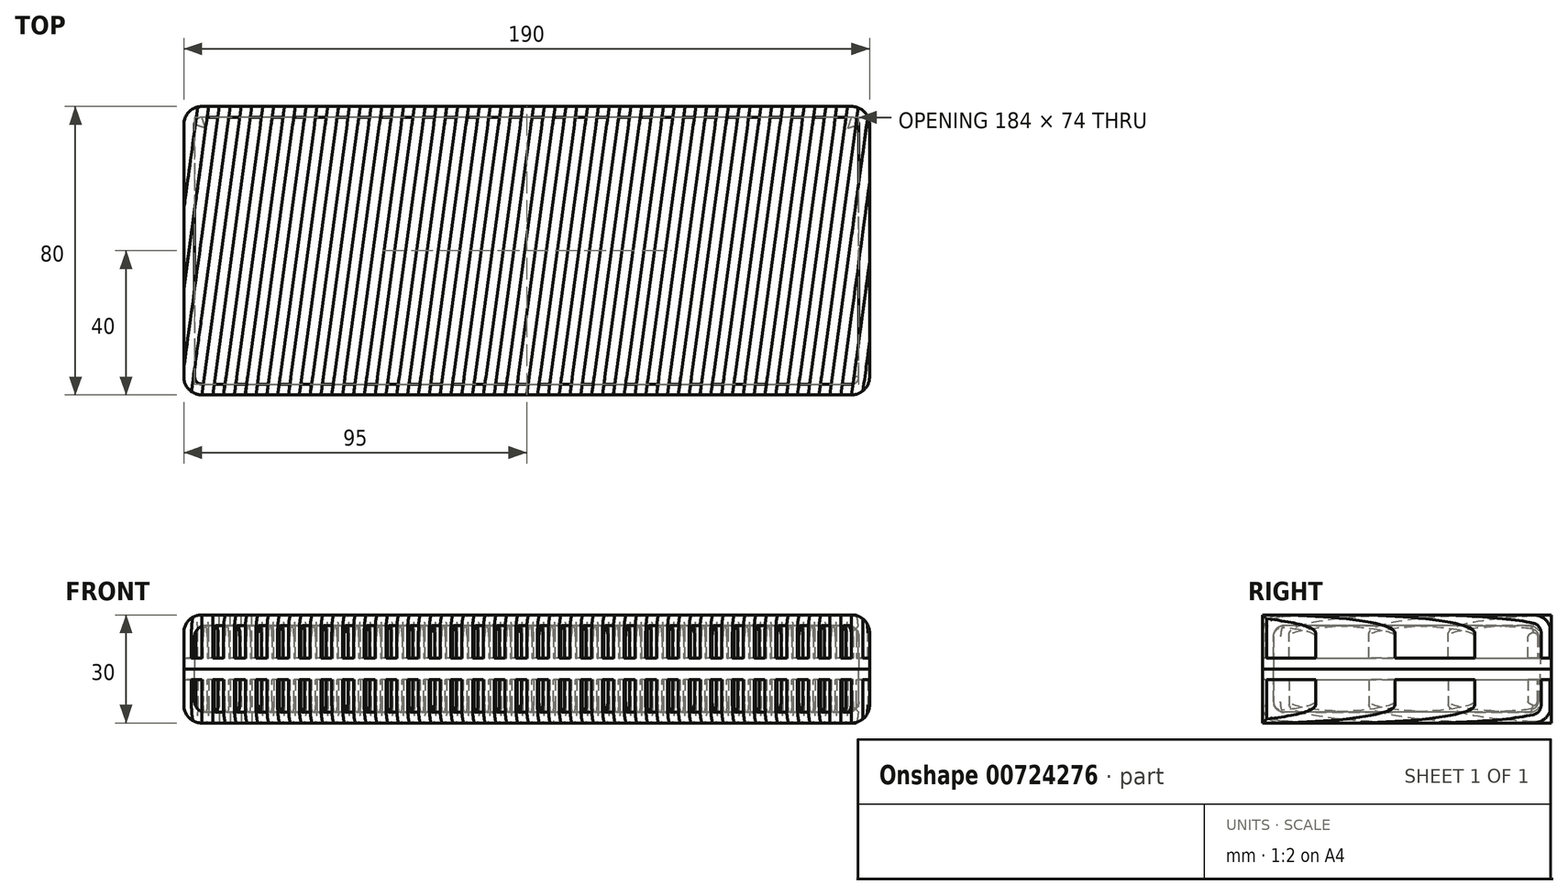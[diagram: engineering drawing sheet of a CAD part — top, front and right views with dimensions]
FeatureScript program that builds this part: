
annotation { "Feature Type Name" : "Feature", "Feature Type Description" : "" }
export const myFeature = defineFeature(function(context is Context, id is Id, definition is map)
    precondition{}
    {
        {
            var Q0;
            Q0=qCreatedBy(makeId("Top.planeOp"),FACE);
            var sketch = newSketch(context, id + "F0", { "sketchPlane" : qUnion([Q0])});
            skLineSegment(sketch, "E0.bottom", {"start": v(90, -40) * mm, "end": v(-90, -40) * mm});
            skLineSegment(sketch, "E0.top", {"start": v(90, 40) * mm, "end": v(-90, 40) * mm});
            skLineSegment(sketch, "E0.left", {"start": v(95, -35) * mm, "end": v(95, 35) * mm});
            skLineSegment(sketch, "E0.right", {"start": v(-95, -35) * mm, "end": v(-95, 35) * mm});
            skPoint(sketch, "E0.middle", {"position": v(0, 0) * mm});
            skPoint(sketch, "E1.visualSharp", {"position": v(-95, 40) * mm});
            skArc(sketch, "E1.filletArc", {"start": v(-90, 40) * mm, "mid": v(-93.54, 38.54) * mm, "end": v(-95, 35) * mm});
            skPoint(sketch, "E2.visualSharp", {"position": v(-95, -40) * mm});
            skArc(sketch, "E2.filletArc", {"start": v(-95, -35) * mm, "mid": v(-93.54, -38.54) * mm, "end": v(-90, -40) * mm});
            skPoint(sketch, "E3.visualSharp", {"position": v(95, -40) * mm});
            skArc(sketch, "E3.filletArc", {"start": v(90, -40) * mm, "mid": v(93.54, -38.54) * mm, "end": v(95, -35) * mm});
            skPoint(sketch, "E4.visualSharp", {"position": v(95, 40) * mm});
            skArc(sketch, "E4.filletArc", {"start": v(95, 35) * mm, "mid": v(93.54, 38.54) * mm, "end": v(90, 40) * mm});
            skSolve(sketch);
        }
        {
            var Q0;
            Q0=makeQuery(id+"F0.imprint","IMPRINT",FACE,{"disambiguationData":[TD([[makeQuery(id+"F0.imprint","IMPRINT",EDGE,{"derivedFrom":sQuery(id+"F0.wireOp",EDGE,"E0.bottom")}),-1.0]])]});
            extrude(context, id + "F1", {"entities" : qUnion([Q0]), "depth" : 15 * mm, "offsetDistance" : 25 * mm});
        }
        {
            var Q0;
            Q0=makeQuery(id+"F1.opExtrude","CAP_FACE",FACE,{"disambiguationData":[OSD([sQuery(id+"F0.wireOp",EDGE,"E0.bottom"),sQuery(id+"F0.wireOp",EDGE,"E0.top"),sQuery(id+"F0.wireOp",EDGE,"E0.left"),sQuery(id+"F0.wireOp",EDGE,"E0.right"),sQuery(id+"F0.wireOp",EDGE,"E1.filletArc"),sQuery(id+"F0.wireOp",EDGE,"E2.filletArc"),sQuery(id+"F0.wireOp",EDGE,"E3.filletArc"),sQuery(id+"F0.wireOp",EDGE,"E4.filletArc")])],"isStart":false});
            var sketch = newSketch(context, id + "F2", { "sketchPlane" : qUnion([Q0])});
            skLineSegment(sketch, "E5.0", {"start": v(92, -35) * mm, "end": v(92, 35) * mm});
            skArc(sketch, "E5.1", {"start": v(90, -37) * mm, "mid": v(91.41, -36.41) * mm, "end": v(92, -35) * mm});
            skArc(sketch, "E5.2", {"start": v(92, 35) * mm, "mid": v(91.41, 36.41) * mm, "end": v(90, 37) * mm});
            skLineSegment(sketch, "E5.3", {"start": v(-90, -37) * mm, "end": v(90, -37) * mm});
            skLineSegment(sketch, "E5.4", {"start": v(90, 37) * mm, "end": v(-90, 37) * mm});
            skArc(sketch, "E5.5", {"start": v(-90, 37) * mm, "mid": v(-91.41, 36.41) * mm, "end": v(-92, 35) * mm});
            skLineSegment(sketch, "E5.6", {"start": v(-92, 35) * mm, "end": v(-92, -35) * mm});
            skArc(sketch, "E5.7", {"start": v(-92, -35) * mm, "mid": v(-91.41, -36.41) * mm, "end": v(-90, -37) * mm});
            skSolve(sketch);
        }
        {
            var Q0;
            Q0=makeQuery(id+"F2.imprint","IMPRINT",FACE,{"disambiguationData":[TD([[makeQuery(id+"F2.imprint","IMPRINT",EDGE,{"derivedFrom":sQuery(id+"F2.wireOp",EDGE,"E5.0")}),1.0]])]});
            extrude(context, id + "F3", {"entities" : qUnion([Q0]), "operationType" : NewBodyOperationType.REMOVE, "oppositeDirection" : true, "depth" : 12 * mm, "offsetDistance" : 25 * mm});
        }
        {
            var Q0;
            Q0=makeQuery(id+"F3.boolean.opBoolean","COPY",EDGE,{"derivedFrom":makeQuery(id+"F3.opExtrude","CAP_EDGE",EDGE,{"disambiguationData":[OSD([sQuery(id+"F2.wireOp",EDGE,"E5.4")])],"isStart":false})});
            var Q1;
            Q1=makeQuery(id+"F3.boolean.opBoolean","COPY",EDGE,{"derivedFrom":makeQuery(id+"F3.opExtrude","CAP_EDGE",EDGE,{"disambiguationData":[OSD([sQuery(id+"F2.wireOp",EDGE,"E5.6")])],"isStart":false})});
            var Q2;
            Q2=makeQuery(id+"F3.boolean.opBoolean","COPY",EDGE,{"derivedFrom":makeQuery(id+"F3.opExtrude","CAP_EDGE",EDGE,{"disambiguationData":[OSD([sQuery(id+"F2.wireOp",EDGE,"E5.3")])],"isStart":false})});
            var Q3;
            Q3=makeQuery(id+"F3.boolean.opBoolean","COPY",EDGE,{"derivedFrom":makeQuery(id+"F3.opExtrude","CAP_EDGE",EDGE,{"disambiguationData":[OSD([sQuery(id+"F2.wireOp",EDGE,"E5.0")])],"isStart":false})});
            fillet(context, id + "F4", {"entities" : qUnion([Q0, Q1, Q2, Q3]), "radius" : 3 * mm, "tangentPropagation" : true, "allowEdgeOverflow" : false});
        }
        {
            var Q0;
            Q0=makeQuery(id+"F3.boolean.opBoolean","COPY",FACE,{"derivedFrom":makeQuery(id+"F3.opExtrude","CAP_FACE",FACE,{"disambiguationData":[OSD([sQuery(id+"F2.wireOp",EDGE,"E5.0"),sQuery(id+"F2.wireOp",EDGE,"E5.1"),sQuery(id+"F2.wireOp",EDGE,"E5.2"),sQuery(id+"F2.wireOp",EDGE,"E5.3"),sQuery(id+"F2.wireOp",EDGE,"E5.4"),sQuery(id+"F2.wireOp",EDGE,"E5.5"),sQuery(id+"F2.wireOp",EDGE,"E5.6"),sQuery(id+"F2.wireOp",EDGE,"E5.7")])],"isStart":false})});
            var sketch = newSketch(context, id + "F5", { "sketchPlane" : qUnion([Q0])});
            skLineSegment(sketch, "E6", {"start": v(89, 0) * mm, "end": v(44.92, 0) * mm, "construction": true});
            skPoint(sketch, "E7", {"position": v(44.92, 0) * mm});
            skCircle(sketch, "E8", {"center": v(44.92, 0) * mm, "radius": 24 * mm, "construction": true});
            skPoint(sketch, "E9", {"position": v(68.93, 0) * mm});
            skLineSegment(sketch, "E10", {"start": v(68.93, 0) * mm, "end": v(65.93, 11.62) * mm, "construction": true});
            skLineSegment(sketch, "E11", {"start": v(65.93, 11.62) * mm, "end": v(57.69, 20.34) * mm, "construction": true});
            skLineSegment(sketch, "E12", {"start": v(57.69, 20.34) * mm, "end": v(46.25, 23.97) * mm, "construction": true});
            skLineSegment(sketch, "E13", {"start": v(46.25, 23.97) * mm, "end": v(34.48, 21.62) * mm, "construction": true});
            skPoint(sketch, "E14", {"position": v(65.93, 11.62) * mm});
            skPoint(sketch, "E15", {"position": v(57.69, 20.34) * mm});
            skPoint(sketch, "E16", {"position": v(46.25, 23.97) * mm});
            skPoint(sketch, "E17", {"position": v(34.48, 21.62) * mm});
            skLineSegment(sketch, "E18.MirrorCS", {"start": v(68.93, 0) * mm, "end": v(65.93, -11.62) * mm, "construction": true});
            skLineSegment(sketch, "E19.MirrorCS", {"start": v(65.93, -11.62) * mm, "end": v(57.69, -20.34) * mm, "construction": true});
            skLineSegment(sketch, "E20.MirrorCS", {"start": v(57.69, -20.34) * mm, "end": v(46.25, -23.97) * mm, "construction": true});
            skLineSegment(sketch, "E21.MirrorCS", {"start": v(46.25, -23.97) * mm, "end": v(34.48, -21.62) * mm, "construction": true});
            skSolve(sketch);
        }
        {
            var Q0;
            {var subQ0=sQuery(id+"F0.wireOp",EDGE,"E1.filletArc");var subQ1=sQuery(id+"F0.wireOp",EDGE,"E0.top");var subQ2=sQuery(id+"F0.wireOp",EDGE,"E0.right");var subQ3=sQuery(id+"F0.wireOp",EDGE,"E0.bottom");var subQ4=sQuery(id+"F0.wireOp",EDGE,"E2.filletArc");Q0=makeQuery(id+"FFGJoZZdiIJdPJ1_1.boolean.opBoolean","SPLIT",FACE,{"disambiguationData":[TD([makeQuery(id+"F1.opExtrude","SWEPT_FACE",FACE,{"disambiguationData":[OSD([subQ2])]})])],"derivedFrom":makeQuery(id+"F1.opExtrude","CAP_FACE",FACE,{"disambiguationData":[OSD([subQ3,subQ1,sQuery(id+"F0.wireOp",EDGE,"E0.left"),subQ2,subQ0,subQ4,sQuery(id+"F0.wireOp",EDGE,"E3.filletArc"),sQuery(id+"F0.wireOp",EDGE,"E4.filletArc")])],"isStart":true})});}
            var sketch = newSketch(context, id + "F6", { "sketchPlane" : qUnion([Q0])});
            skLineSegment(sketch, "E22", {"start": v(-90, 40) * mm, "end": v(-79.12, -40) * mm});
            skLineSegment(sketch, "E23.1.0.0", {"start": v(-87, 40) * mm, "end": v(-76.12, -40) * mm});
            skLineSegment(sketch, "E23.2.0.0", {"start": v(-84, 40) * mm, "end": v(-73.12, -40) * mm});
            skLineSegment(sketch, "E23.3.0.0", {"start": v(-81, 40) * mm, "end": v(-70.12, -40) * mm});
            skLineSegment(sketch, "E23.4.0.0", {"start": v(-78, 40) * mm, "end": v(-67.12, -40) * mm});
            skLineSegment(sketch, "E23.5.0.0", {"start": v(-75, 40) * mm, "end": v(-64.12, -40) * mm});
            skLineSegment(sketch, "E23.6.0.0", {"start": v(-72, 40) * mm, "end": v(-61.12, -40) * mm});
            skLineSegment(sketch, "E23.7.0.0", {"start": v(-69, 40) * mm, "end": v(-58.12, -40) * mm});
            skLineSegment(sketch, "E23.8.0.0", {"start": v(-66, 40) * mm, "end": v(-55.12, -40) * mm});
            skLineSegment(sketch, "E23.9.0.0", {"start": v(-63, 40) * mm, "end": v(-52.12, -40) * mm});
            skLineSegment(sketch, "E23.10.0.0", {"start": v(-60, 40) * mm, "end": v(-49.12, -40) * mm});
            skLineSegment(sketch, "E23.11.0.0", {"start": v(-57, 40) * mm, "end": v(-46.12, -40) * mm});
            skLineSegment(sketch, "E23.12.0.0", {"start": v(-54, 40) * mm, "end": v(-43.12, -40) * mm});
            skLineSegment(sketch, "E23.13.0.0", {"start": v(-51, 40) * mm, "end": v(-40.12, -40) * mm});
            skLineSegment(sketch, "E23.14.0.0", {"start": v(-48, 40) * mm, "end": v(-37.12, -40) * mm});
            skLineSegment(sketch, "E23.15.0.0", {"start": v(-45, 40) * mm, "end": v(-34.12, -40) * mm});
            skLineSegment(sketch, "E23.16.0.0", {"start": v(-42, 40) * mm, "end": v(-31.12, -40) * mm});
            skLineSegment(sketch, "E23.17.0.0", {"start": v(-39, 40) * mm, "end": v(-28.12, -40) * mm});
            skLineSegment(sketch, "E23.18.0.0", {"start": v(-36, 40) * mm, "end": v(-25.12, -40) * mm});
            skLineSegment(sketch, "E23.19.0.0", {"start": v(-33, 40) * mm, "end": v(-22.12, -40) * mm});
            skLineSegment(sketch, "E23.direction1", {"start": v(-79.12, -40) * mm, "end": v(-76.12, -40) * mm, "construction": true});
            skLineSegment(sketch, "E24.0.20.0", {"start": v(-30, 40) * mm, "end": v(-19.12, -40) * mm});
            skLineSegment(sketch, "E24.0.21.0", {"start": v(-27, 40) * mm, "end": v(-16.12, -40) * mm});
            skLineSegment(sketch, "E24.0.22.0", {"start": v(-24, 40) * mm, "end": v(-13.12, -40) * mm});
            skLineSegment(sketch, "E24.0.23.0", {"start": v(-21, 40) * mm, "end": v(-10.12, -40) * mm});
            skLineSegment(sketch, "E24.0.24.0", {"start": v(-18, 40) * mm, "end": v(-7.12, -40) * mm});
            skLineSegment(sketch, "E24.0.25.0", {"start": v(-15, 40) * mm, "end": v(-4.12, -40) * mm});
            skLineSegment(sketch, "E24.0.26.0", {"start": v(-12, 40) * mm, "end": v(-1.12, -40) * mm});
            skLineSegment(sketch, "E24.0.27.0", {"start": v(-9, 40) * mm, "end": v(1.88, -40) * mm});
            skLineSegment(sketch, "E24.0.28.0", {"start": v(-6, 40) * mm, "end": v(4.88, -40) * mm});
            skLineSegment(sketch, "E24.0.29.0", {"start": v(-3, 40) * mm, "end": v(7.88, -40) * mm});
            skLineSegment(sketch, "E24.0.30.0", {"start": v(0, 40) * mm, "end": v(10.88, -40) * mm});
            skLineSegment(sketch, "E24.0.31.0", {"start": v(3, 40) * mm, "end": v(13.88, -40) * mm});
            skLineSegment(sketch, "E24.0.32.0", {"start": v(6, 40) * mm, "end": v(16.88, -40) * mm});
            skLineSegment(sketch, "E24.0.33.0", {"start": v(9, 40) * mm, "end": v(19.88, -40) * mm});
            skLineSegment(sketch, "E24.0.34.0", {"start": v(12, 40) * mm, "end": v(22.88, -40) * mm});
            skLineSegment(sketch, "E24.0.35.0", {"start": v(15, 40) * mm, "end": v(25.88, -40) * mm});
            skLineSegment(sketch, "E24.0.36.0", {"start": v(18, 40) * mm, "end": v(28.88, -40) * mm});
            skLineSegment(sketch, "E24.0.37.0", {"start": v(21, 40) * mm, "end": v(31.88, -40) * mm});
            skLineSegment(sketch, "E24.0.38.0", {"start": v(24, 40) * mm, "end": v(34.88, -40) * mm});
            skLineSegment(sketch, "E24.0.39.0", {"start": v(27, 40) * mm, "end": v(37.88, -40) * mm});
            skLineSegment(sketch, "E24.0.40.0", {"start": v(30, 40) * mm, "end": v(40.88, -40) * mm});
            skLineSegment(sketch, "E24.0.41.0", {"start": v(33, 40) * mm, "end": v(43.88, -40) * mm});
            skLineSegment(sketch, "E24.0.42.0", {"start": v(36, 40) * mm, "end": v(46.88, -40) * mm});
            skLineSegment(sketch, "E24.0.43.0", {"start": v(39, 40) * mm, "end": v(49.88, -40) * mm});
            skLineSegment(sketch, "E24.0.44.0", {"start": v(42, 40) * mm, "end": v(52.88, -40) * mm});
            skLineSegment(sketch, "E24.0.45.0", {"start": v(45, 40) * mm, "end": v(55.88, -40) * mm});
            skLineSegment(sketch, "E24.0.46.0", {"start": v(48, 40) * mm, "end": v(58.88, -40) * mm});
            skLineSegment(sketch, "E24.0.47.0", {"start": v(51, 40) * mm, "end": v(61.88, -40) * mm});
            skLineSegment(sketch, "E24.0.48.0", {"start": v(54, 40) * mm, "end": v(64.88, -40) * mm});
            skLineSegment(sketch, "E24.0.49.0", {"start": v(57, 40) * mm, "end": v(67.88, -40) * mm});
            skLineSegment(sketch, "E24.0.50.0", {"start": v(60, 40) * mm, "end": v(70.88, -40) * mm});
            skLineSegment(sketch, "E24.0.51.0", {"start": v(63, 40) * mm, "end": v(73.88, -40) * mm});
            skLineSegment(sketch, "E24.0.52.0", {"start": v(66, 40) * mm, "end": v(76.88, -40) * mm});
            skLineSegment(sketch, "E24.0.53.0", {"start": v(69, 40) * mm, "end": v(79.88, -40) * mm});
            skLineSegment(sketch, "E24.0.54.0", {"start": v(72, 40) * mm, "end": v(82.88, -40) * mm});
            skLineSegment(sketch, "E24.0.55.0", {"start": v(75, 40) * mm, "end": v(85.88, -40) * mm});
            skLineSegment(sketch, "E24.0.56.0", {"start": v(78, 40) * mm, "end": v(88.88, -40) * mm});
            skLineSegment(sketch, "E24.0.57.0", {"start": v(81, 40) * mm, "end": v(91.88, -40) * mm});
            skLineSegment(sketch, "E24.0.58.0", {"start": v(84, 40) * mm, "end": v(94.88, -40) * mm});
            skLineSegment(sketch, "E24.0.59.0", {"start": v(87, 40) * mm, "end": v(97.88, -40) * mm});
            skLineSegment(sketch, "E25.1.0.0", {"start": v(-93, 40) * mm, "end": v(-82.12, -40) * mm});
            skLineSegment(sketch, "E25.2.0.0", {"start": v(-96, 40) * mm, "end": v(-85.12, -40) * mm});
            skLineSegment(sketch, "E25.direction1", {"start": v(-79.12, -40) * mm, "end": v(-82.12, -40) * mm, "construction": true});
            skLineSegment(sketch, "E26.0.60.0", {"start": v(90, 40) * mm, "end": v(100.88, -40) * mm});
            skLineSegment(sketch, "E26.0.61.0", {"start": v(93, 40) * mm, "end": v(103.88, -40) * mm});
            skLineSegment(sketch, "E27.0.3.0", {"start": v(-99, 40) * mm, "end": v(-88.12, -40) * mm});
            skLineSegment(sketch, "E27.0.4.0", {"start": v(-102, 40) * mm, "end": v(-91.12, -40) * mm});
            skSolve(sketch);
        }
        {
            var Q0;
            {var subQ0=sQuery(id+"F6.wireOp",EDGE,"E23.1.0.0");Q0=makeQuery(id+"F6.imprint","IMPRINT",FACE,{"disambiguationData":[TD([[makeQuery(id+"F6.imprint","IMPRINT",EDGE,{"derivedFrom":subQ0}),1.0]])]});}
            var Q1;
            {var subQ0=sQuery(id+"F6.wireOp",EDGE,"E23.3.0.0");Q1=makeQuery(id+"F6.imprint","IMPRINT",FACE,{"disambiguationData":[TD([[makeQuery(id+"F6.imprint","IMPRINT",EDGE,{"derivedFrom":subQ0}),1.0]])]});}
            var Q2;
            {var subQ0=sQuery(id+"F6.wireOp",EDGE,"E23.5.0.0");Q2=makeQuery(id+"F6.imprint","IMPRINT",FACE,{"disambiguationData":[TD([[makeQuery(id+"F6.imprint","IMPRINT",EDGE,{"derivedFrom":subQ0}),1.0]])]});}
            var Q3;
            {var subQ0=sQuery(id+"F6.wireOp",EDGE,"E23.7.0.0");Q3=makeQuery(id+"F6.imprint","IMPRINT",FACE,{"disambiguationData":[TD([[makeQuery(id+"F6.imprint","IMPRINT",EDGE,{"derivedFrom":subQ0}),1.0]])]});}
            var Q4;
            {var subQ0=sQuery(id+"F6.wireOp",EDGE,"E23.9.0.0");Q4=makeQuery(id+"F6.imprint","IMPRINT",FACE,{"disambiguationData":[TD([[makeQuery(id+"F6.imprint","IMPRINT",EDGE,{"derivedFrom":subQ0}),1.0]])]});}
            var Q5;
            {var subQ0=sQuery(id+"F6.wireOp",EDGE,"E23.11.0.0");Q5=makeQuery(id+"F6.imprint","IMPRINT",FACE,{"disambiguationData":[TD([[makeQuery(id+"F6.imprint","IMPRINT",EDGE,{"derivedFrom":subQ0}),1.0]])]});}
            var Q6;
            {var subQ0=sQuery(id+"F6.wireOp",EDGE,"E23.13.0.0");Q6=makeQuery(id+"F6.imprint","IMPRINT",FACE,{"disambiguationData":[TD([[makeQuery(id+"F6.imprint","IMPRINT",EDGE,{"derivedFrom":subQ0}),1.0]])]});}
            var Q7;
            {var subQ0=sQuery(id+"F6.wireOp",EDGE,"E23.15.0.0");Q7=makeQuery(id+"F6.imprint","IMPRINT",FACE,{"disambiguationData":[TD([[makeQuery(id+"F6.imprint","IMPRINT",EDGE,{"derivedFrom":subQ0}),1.0]])]});}
            var Q8;
            {var subQ0=sQuery(id+"F6.wireOp",EDGE,"E23.17.0.0");Q8=makeQuery(id+"F6.imprint","IMPRINT",FACE,{"disambiguationData":[TD([[makeQuery(id+"F6.imprint","IMPRINT",EDGE,{"derivedFrom":subQ0}),1.0]])]});}
            var Q9;
            {var subQ0=sQuery(id+"F6.wireOp",EDGE,"E23.19.0.0");Q9=makeQuery(id+"F6.imprint","IMPRINT",FACE,{"disambiguationData":[TD([[makeQuery(id+"F6.imprint","IMPRINT",EDGE,{"derivedFrom":subQ0}),1.0]])]});}
            var Q10;
            {var subQ0=sQuery(id+"F6.wireOp",EDGE,"E24.0.21.0");Q10=makeQuery(id+"F6.imprint","IMPRINT",FACE,{"disambiguationData":[TD([[makeQuery(id+"F6.imprint","IMPRINT",EDGE,{"derivedFrom":subQ0}),1.0]])]});}
            var Q11;
            {var subQ0=sQuery(id+"F6.wireOp",EDGE,"E24.0.23.0");Q11=makeQuery(id+"F6.imprint","IMPRINT",FACE,{"disambiguationData":[TD([[makeQuery(id+"F6.imprint","IMPRINT",EDGE,{"derivedFrom":subQ0}),1.0]])]});}
            var Q12;
            {var subQ0=sQuery(id+"F6.wireOp",EDGE,"E24.0.25.0");Q12=makeQuery(id+"F6.imprint","IMPRINT",FACE,{"disambiguationData":[TD([[makeQuery(id+"F6.imprint","IMPRINT",EDGE,{"derivedFrom":subQ0}),1.0]])]});}
            var Q13;
            {var subQ0=sQuery(id+"F6.wireOp",EDGE,"E24.0.27.0");Q13=makeQuery(id+"F6.imprint","IMPRINT",FACE,{"disambiguationData":[TD([[makeQuery(id+"F6.imprint","IMPRINT",EDGE,{"derivedFrom":subQ0}),1.0]])]});}
            var Q14;
            {var subQ0=sQuery(id+"F6.wireOp",EDGE,"E24.0.29.0");Q14=makeQuery(id+"F6.imprint","IMPRINT",FACE,{"disambiguationData":[TD([[makeQuery(id+"F6.imprint","IMPRINT",EDGE,{"derivedFrom":subQ0}),1.0]])]});}
            var Q15;
            {var subQ0=sQuery(id+"F6.wireOp",EDGE,"E24.0.31.0");Q15=makeQuery(id+"F6.imprint","IMPRINT",FACE,{"disambiguationData":[TD([[makeQuery(id+"F6.imprint","IMPRINT",EDGE,{"derivedFrom":subQ0}),1.0]])]});}
            var Q16;
            {var subQ0=sQuery(id+"F6.wireOp",EDGE,"E24.0.33.0");Q16=makeQuery(id+"F6.imprint","IMPRINT",FACE,{"disambiguationData":[TD([[makeQuery(id+"F6.imprint","IMPRINT",EDGE,{"derivedFrom":subQ0}),1.0]])]});}
            var Q17;
            {var subQ0=sQuery(id+"F6.wireOp",EDGE,"E24.0.35.0");Q17=makeQuery(id+"F6.imprint","IMPRINT",FACE,{"disambiguationData":[TD([[makeQuery(id+"F6.imprint","IMPRINT",EDGE,{"derivedFrom":subQ0}),1.0]])]});}
            var Q18;
            {var subQ0=sQuery(id+"F6.wireOp",EDGE,"E24.0.37.0");Q18=makeQuery(id+"F6.imprint","IMPRINT",FACE,{"disambiguationData":[TD([[makeQuery(id+"F6.imprint","IMPRINT",EDGE,{"derivedFrom":subQ0}),1.0]])]});}
            var Q19;
            {var subQ0=sQuery(id+"F6.wireOp",EDGE,"E24.0.39.0");Q19=makeQuery(id+"F6.imprint","IMPRINT",FACE,{"disambiguationData":[TD([[makeQuery(id+"F6.imprint","IMPRINT",EDGE,{"derivedFrom":subQ0}),1.0]])]});}
            var Q20;
            {var subQ0=sQuery(id+"F6.wireOp",EDGE,"E24.0.41.0");Q20=makeQuery(id+"F6.imprint","IMPRINT",FACE,{"disambiguationData":[TD([[makeQuery(id+"F6.imprint","IMPRINT",EDGE,{"derivedFrom":subQ0}),1.0]])]});}
            var Q21;
            {var subQ0=sQuery(id+"F6.wireOp",EDGE,"E24.0.43.0");Q21=makeQuery(id+"F6.imprint","IMPRINT",FACE,{"disambiguationData":[TD([[makeQuery(id+"F6.imprint","IMPRINT",EDGE,{"derivedFrom":subQ0}),1.0]])]});}
            var Q22;
            {var subQ0=sQuery(id+"F6.wireOp",EDGE,"E24.0.45.0");Q22=makeQuery(id+"F6.imprint","IMPRINT",FACE,{"disambiguationData":[TD([[makeQuery(id+"F6.imprint","IMPRINT",EDGE,{"derivedFrom":subQ0}),1.0]])]});}
            var Q23;
            {var subQ0=sQuery(id+"F6.wireOp",EDGE,"E24.0.47.0");Q23=makeQuery(id+"F6.imprint","IMPRINT",FACE,{"disambiguationData":[TD([[makeQuery(id+"F6.imprint","IMPRINT",EDGE,{"derivedFrom":subQ0}),1.0]])]});}
            var Q24;
            {var subQ0=sQuery(id+"F6.wireOp",EDGE,"E24.0.49.0");Q24=makeQuery(id+"F6.imprint","IMPRINT",FACE,{"disambiguationData":[TD([[makeQuery(id+"F6.imprint","IMPRINT",EDGE,{"derivedFrom":subQ0}),1.0]])]});}
            var Q25;
            {var subQ0=sQuery(id+"F6.wireOp",EDGE,"E24.0.51.0");Q25=makeQuery(id+"F6.imprint","IMPRINT",FACE,{"disambiguationData":[TD([[makeQuery(id+"F6.imprint","IMPRINT",EDGE,{"derivedFrom":subQ0}),1.0]])]});}
            var Q26;
            {var subQ0=sQuery(id+"F6.wireOp",EDGE,"E24.0.53.0");Q26=makeQuery(id+"F6.imprint","IMPRINT",FACE,{"disambiguationData":[TD([[makeQuery(id+"F6.imprint","IMPRINT",EDGE,{"derivedFrom":subQ0}),1.0]])]});}
            var Q27;
            {var subQ0=sQuery(id+"F6.wireOp",EDGE,"E24.0.55.0");Q27=makeQuery(id+"F6.imprint","IMPRINT",FACE,{"disambiguationData":[TD([[makeQuery(id+"F6.imprint","IMPRINT",EDGE,{"derivedFrom":subQ0}),1.0]])]});}
            var Q28;
            {var subQ0=sQuery(id+"F6.wireOp",EDGE,"E24.0.57.0");var subQ1=makeQuery(id+"F1.opExtrude","CAP_EDGE",EDGE,{"disambiguationData":[OSD([sQuery(id+"F0.wireOp",EDGE,"E0.bottom")])],"isStart":true});var subQ2=makeQuery(id+"F6.imprint","INTERSECT",VERTEX,{"derivedFrom":[subQ1,subQ0]});Q28=makeQuery(id+"F6.imprint","IMPRINT",FACE,{"disambiguationData":[TD([[makeQuery(id+"F6.imprint","IMPRINT",EDGE,{"disambiguationData":[TD([[subQ2,-1.0]])],"derivedFrom":subQ0}),1.0]])]});}
            var Q29;
            {var subQ0=sQuery(id+"F6.wireOp",EDGE,"E22");Q29=makeQuery(id+"F6.imprint","IMPRINT",FACE,{"disambiguationData":[TD([[makeQuery(id+"F6.imprint","IMPRINT",EDGE,{"derivedFrom":subQ0}),-1.0]])]});}
            var Q30;
            {var subQ0=sQuery(id+"F6.wireOp",EDGE,"E25.2.0.0");var subQ1=makeQuery(id+"F1.opExtrude","CAP_EDGE",EDGE,{"disambiguationData":[OSD([sQuery(id+"F0.wireOp",EDGE,"E0.top")])],"isStart":true});var subQ2=makeQuery(id+"F6.imprint","INTERSECT",VERTEX,{"derivedFrom":[subQ1,subQ0]});Q30=makeQuery(id+"F6.imprint","IMPRINT",FACE,{"disambiguationData":[TD([[makeQuery(id+"F6.imprint","IMPRINT",EDGE,{"disambiguationData":[TD([[subQ2,1.0]])],"derivedFrom":subQ0}),-1.0]])]});}
            var Q31;
            {var subQ0=sQuery(id+"F6.wireOp",EDGE,"E27.0.4.0");var subQ1=makeQuery(id+"F1.opExtrude","CAP_EDGE",EDGE,{"disambiguationData":[OSD([sQuery(id+"F0.wireOp",EDGE,"E1.filletArc")])],"isStart":true});var subQ2=makeQuery(id+"F6.imprint","INTERSECT",VERTEX,{"derivedFrom":[subQ1,subQ0]});Q31=makeQuery(id+"F6.imprint","IMPRINT",FACE,{"disambiguationData":[TD([[makeQuery(id+"F6.imprint","IMPRINT",EDGE,{"disambiguationData":[TD([[subQ2,1.0]])],"derivedFrom":subQ0}),-1.0]])]});}
            var Q32;
            {var subQ0=sQuery(id+"F6.wireOp",EDGE,"E24.0.59.0");var subQ1=makeQuery(id+"F1.opExtrude","CAP_EDGE",EDGE,{"disambiguationData":[OSD([sQuery(id+"F0.wireOp",EDGE,"E0.bottom")])],"isStart":true});var subQ2=makeQuery(id+"F6.imprint","INTERSECT",VERTEX,{"derivedFrom":[subQ1,subQ0]});Q32=makeQuery(id+"F6.imprint","IMPRINT",FACE,{"disambiguationData":[TD([[makeQuery(id+"F6.imprint","IMPRINT",EDGE,{"disambiguationData":[TD([[subQ2,-1.0]])],"derivedFrom":subQ0}),1.0]])]});}
            var Q33;
            {var subQ0=sQuery(id+"F6.wireOp",EDGE,"E26.0.61.0");var subQ1=makeQuery(id+"F1.opExtrude","CAP_EDGE",EDGE,{"disambiguationData":[OSD([sQuery(id+"F0.wireOp",EDGE,"E3.filletArc")])],"isStart":true});var subQ2=makeQuery(id+"F6.imprint","INTERSECT",VERTEX,{"derivedFrom":[subQ1,subQ0]});Q33=makeQuery(id+"F6.imprint","IMPRINT",FACE,{"disambiguationData":[TD([[makeQuery(id+"F6.imprint","IMPRINT",EDGE,{"disambiguationData":[TD([[subQ2,-1.0]])],"derivedFrom":subQ0}),1.0]])]});}
            extrude(context, id + "F7", {"entities" : qUnion([Q0, Q1, Q2, Q3, Q4, Q5, Q6, Q7, Q8, Q9, Q10, Q11, Q12, Q13, Q14, Q15, Q16, Q17, Q18, Q19, Q20, Q21, Q22, Q23, Q24, Q25, Q26, Q27, Q28, Q29, Q30, Q31, Q32, Q33]), "operationType" : NewBodyOperationType.REMOVE, "oppositeDirection" : true, "depth" : 12 * mm, "offsetDistance" : 25 * mm});
        }
        {
            var Q0;
            {var subQ0=sQuery(id+"F0.wireOp",EDGE,"E0.bottom");Q0=makeQuery(id+"F7.boolean.opBoolean","SPLIT",EDGE,{"disambiguationData":[TD([makeQuery(id+"F7.opExtrude","SWEPT_FACE",FACE,{"disambiguationData":[OSD([sQuery(id+"F6.wireOp",EDGE,"E23.2.0.0")])]})])],"derivedFrom":makeQuery(id+"F1.opExtrude","CAP_EDGE",EDGE,{"disambiguationData":[OSD([subQ0])],"isStart":true})});}
            var Q1;
            {var subQ0=sQuery(id+"F0.wireOp",EDGE,"E0.bottom");Q1=makeQuery(id+"F7.boolean.opBoolean","SPLIT",EDGE,{"disambiguationData":[TD([makeQuery(id+"F7.opExtrude","SWEPT_FACE",FACE,{"disambiguationData":[OSD([sQuery(id+"F6.wireOp",EDGE,"E23.4.0.0")])]})])],"derivedFrom":makeQuery(id+"F1.opExtrude","CAP_EDGE",EDGE,{"disambiguationData":[OSD([subQ0])],"isStart":true})});}
            var Q2;
            {var subQ0=sQuery(id+"F0.wireOp",EDGE,"E0.bottom");Q2=makeQuery(id+"F7.boolean.opBoolean","SPLIT",EDGE,{"disambiguationData":[TD([makeQuery(id+"F7.opExtrude","SWEPT_FACE",FACE,{"disambiguationData":[OSD([sQuery(id+"F6.wireOp",EDGE,"E23.6.0.0")])]})])],"derivedFrom":makeQuery(id+"F1.opExtrude","CAP_EDGE",EDGE,{"disambiguationData":[OSD([subQ0])],"isStart":true})});}
            var Q3;
            {var subQ0=sQuery(id+"F0.wireOp",EDGE,"E0.bottom");Q3=makeQuery(id+"F7.boolean.opBoolean","SPLIT",EDGE,{"disambiguationData":[TD([makeQuery(id+"F7.opExtrude","SWEPT_FACE",FACE,{"disambiguationData":[OSD([sQuery(id+"F6.wireOp",EDGE,"E23.8.0.0")])]})])],"derivedFrom":makeQuery(id+"F1.opExtrude","CAP_EDGE",EDGE,{"disambiguationData":[OSD([subQ0])],"isStart":true})});}
            var Q4;
            {var subQ0=sQuery(id+"F0.wireOp",EDGE,"E0.bottom");Q4=makeQuery(id+"F7.boolean.opBoolean","SPLIT",EDGE,{"disambiguationData":[TD([makeQuery(id+"F7.opExtrude","SWEPT_FACE",FACE,{"disambiguationData":[OSD([sQuery(id+"F6.wireOp",EDGE,"E23.10.0.0")])]})])],"derivedFrom":makeQuery(id+"F1.opExtrude","CAP_EDGE",EDGE,{"disambiguationData":[OSD([subQ0])],"isStart":true})});}
            var Q5;
            {var subQ0=sQuery(id+"F0.wireOp",EDGE,"E0.bottom");var subQ1=sQuery(id+"F0.wireOp",EDGE,"E2.filletArc");Q5=makeQuery(id+"F7.boolean.opBoolean","SPLIT",EDGE,{"disambiguationData":[TD([makeQuery(id+"F1.opExtrude","SWEPT_FACE",FACE,{"disambiguationData":[OSD([subQ1])]})])],"derivedFrom":makeQuery(id+"F1.opExtrude","CAP_EDGE",EDGE,{"disambiguationData":[OSD([subQ0])],"isStart":true})});}
            var Q6;
            Q6=makeQuery(id+"F1.opExtrude","CAP_EDGE",EDGE,{"disambiguationData":[OSD([sQuery(id+"F0.wireOp",EDGE,"E0.right")])],"isStart":true});
            var Q7;
            {var subQ0=sQuery(id+"F0.wireOp",EDGE,"E1.filletArc");var subQ1=sQuery(id+"F0.wireOp",EDGE,"E0.top");Q7=makeQuery(id+"F7.boolean.opBoolean","SPLIT",EDGE,{"disambiguationData":[TD([makeQuery(id+"F1.opExtrude","SWEPT_FACE",FACE,{"disambiguationData":[OSD([subQ0])]})])],"derivedFrom":makeQuery(id+"F1.opExtrude","CAP_EDGE",EDGE,{"disambiguationData":[OSD([subQ1])],"isStart":true})});}
            var Q8;
            {var subQ0=sQuery(id+"F0.wireOp",EDGE,"E0.bottom");Q8=makeQuery(id+"F7.boolean.opBoolean","SPLIT",EDGE,{"disambiguationData":[TD([makeQuery(id+"F7.opExtrude","SWEPT_FACE",FACE,{"disambiguationData":[OSD([sQuery(id+"F6.wireOp",EDGE,"E23.12.0.0")])]})])],"derivedFrom":makeQuery(id+"F1.opExtrude","CAP_EDGE",EDGE,{"disambiguationData":[OSD([subQ0])],"isStart":true})});}
            var Q9;
            {var subQ0=sQuery(id+"F0.wireOp",EDGE,"E0.bottom");Q9=makeQuery(id+"F7.boolean.opBoolean","SPLIT",EDGE,{"disambiguationData":[TD([makeQuery(id+"F7.opExtrude","SWEPT_FACE",FACE,{"disambiguationData":[OSD([sQuery(id+"F6.wireOp",EDGE,"E23.14.0.0")])]})])],"derivedFrom":makeQuery(id+"F1.opExtrude","CAP_EDGE",EDGE,{"disambiguationData":[OSD([subQ0])],"isStart":true})});}
            var Q10;
            {var subQ0=sQuery(id+"F0.wireOp",EDGE,"E0.bottom");Q10=makeQuery(id+"F7.boolean.opBoolean","SPLIT",EDGE,{"disambiguationData":[TD([makeQuery(id+"F7.opExtrude","SWEPT_FACE",FACE,{"disambiguationData":[OSD([sQuery(id+"F6.wireOp",EDGE,"E23.16.0.0")])]})])],"derivedFrom":makeQuery(id+"F1.opExtrude","CAP_EDGE",EDGE,{"disambiguationData":[OSD([subQ0])],"isStart":true})});}
            var Q11;
            {var subQ0=sQuery(id+"F0.wireOp",EDGE,"E0.bottom");Q11=makeQuery(id+"F7.boolean.opBoolean","SPLIT",EDGE,{"disambiguationData":[TD([makeQuery(id+"F7.opExtrude","SWEPT_FACE",FACE,{"disambiguationData":[OSD([sQuery(id+"F6.wireOp",EDGE,"E23.18.0.0")])]})])],"derivedFrom":makeQuery(id+"F1.opExtrude","CAP_EDGE",EDGE,{"disambiguationData":[OSD([subQ0])],"isStart":true})});}
            var Q12;
            {var subQ0=sQuery(id+"F0.wireOp",EDGE,"E0.bottom");Q12=makeQuery(id+"F7.boolean.opBoolean","SPLIT",EDGE,{"disambiguationData":[TD([makeQuery(id+"F7.opExtrude","SWEPT_FACE",FACE,{"disambiguationData":[OSD([sQuery(id+"F6.wireOp",EDGE,"E24.0.20.0")])]})])],"derivedFrom":makeQuery(id+"F1.opExtrude","CAP_EDGE",EDGE,{"disambiguationData":[OSD([subQ0])],"isStart":true})});}
            var Q13;
            {var subQ0=sQuery(id+"F0.wireOp",EDGE,"E0.bottom");Q13=makeQuery(id+"F7.boolean.opBoolean","SPLIT",EDGE,{"disambiguationData":[TD([makeQuery(id+"F7.opExtrude","SWEPT_FACE",FACE,{"disambiguationData":[OSD([sQuery(id+"F6.wireOp",EDGE,"E24.0.22.0")])]})])],"derivedFrom":makeQuery(id+"F1.opExtrude","CAP_EDGE",EDGE,{"disambiguationData":[OSD([subQ0])],"isStart":true})});}
            var Q14;
            {var subQ0=sQuery(id+"F0.wireOp",EDGE,"E0.bottom");Q14=makeQuery(id+"F7.boolean.opBoolean","SPLIT",EDGE,{"disambiguationData":[TD([makeQuery(id+"F7.opExtrude","SWEPT_FACE",FACE,{"disambiguationData":[OSD([sQuery(id+"F6.wireOp",EDGE,"E24.0.24.0")])]})])],"derivedFrom":makeQuery(id+"F1.opExtrude","CAP_EDGE",EDGE,{"disambiguationData":[OSD([subQ0])],"isStart":true})});}
            var Q15;
            {var subQ0=sQuery(id+"F0.wireOp",EDGE,"E0.bottom");Q15=makeQuery(id+"F7.boolean.opBoolean","SPLIT",EDGE,{"disambiguationData":[TD([makeQuery(id+"F7.opExtrude","SWEPT_FACE",FACE,{"disambiguationData":[OSD([sQuery(id+"F6.wireOp",EDGE,"E24.0.26.0")])]})])],"derivedFrom":makeQuery(id+"F1.opExtrude","CAP_EDGE",EDGE,{"disambiguationData":[OSD([subQ0])],"isStart":true})});}
            var Q16;
            {var subQ0=sQuery(id+"F0.wireOp",EDGE,"E0.bottom");Q16=makeQuery(id+"F7.boolean.opBoolean","SPLIT",EDGE,{"disambiguationData":[TD([makeQuery(id+"F7.opExtrude","SWEPT_FACE",FACE,{"disambiguationData":[OSD([sQuery(id+"F6.wireOp",EDGE,"E24.0.28.0")])]})])],"derivedFrom":makeQuery(id+"F1.opExtrude","CAP_EDGE",EDGE,{"disambiguationData":[OSD([subQ0])],"isStart":true})});}
            var Q17;
            {var subQ0=sQuery(id+"F0.wireOp",EDGE,"E0.bottom");Q17=makeQuery(id+"F7.boolean.opBoolean","SPLIT",EDGE,{"disambiguationData":[TD([makeQuery(id+"F7.opExtrude","SWEPT_FACE",FACE,{"disambiguationData":[OSD([sQuery(id+"F6.wireOp",EDGE,"E24.0.30.0")])]})])],"derivedFrom":makeQuery(id+"F1.opExtrude","CAP_EDGE",EDGE,{"disambiguationData":[OSD([subQ0])],"isStart":true})});}
            var Q18;
            {var subQ0=sQuery(id+"F0.wireOp",EDGE,"E0.bottom");Q18=makeQuery(id+"F7.boolean.opBoolean","SPLIT",EDGE,{"disambiguationData":[TD([makeQuery(id+"F7.opExtrude","SWEPT_FACE",FACE,{"disambiguationData":[OSD([sQuery(id+"F6.wireOp",EDGE,"E24.0.32.0")])]})])],"derivedFrom":makeQuery(id+"F1.opExtrude","CAP_EDGE",EDGE,{"disambiguationData":[OSD([subQ0])],"isStart":true})});}
            var Q19;
            {var subQ0=sQuery(id+"F0.wireOp",EDGE,"E0.bottom");Q19=makeQuery(id+"F7.boolean.opBoolean","SPLIT",EDGE,{"disambiguationData":[TD([makeQuery(id+"F7.opExtrude","SWEPT_FACE",FACE,{"disambiguationData":[OSD([sQuery(id+"F6.wireOp",EDGE,"E24.0.34.0")])]})])],"derivedFrom":makeQuery(id+"F1.opExtrude","CAP_EDGE",EDGE,{"disambiguationData":[OSD([subQ0])],"isStart":true})});}
            var Q20;
            {var subQ0=sQuery(id+"F0.wireOp",EDGE,"E0.bottom");Q20=makeQuery(id+"F7.boolean.opBoolean","SPLIT",EDGE,{"disambiguationData":[TD([makeQuery(id+"F7.opExtrude","SWEPT_FACE",FACE,{"disambiguationData":[OSD([sQuery(id+"F6.wireOp",EDGE,"E24.0.36.0")])]})])],"derivedFrom":makeQuery(id+"F1.opExtrude","CAP_EDGE",EDGE,{"disambiguationData":[OSD([subQ0])],"isStart":true})});}
            var Q21;
            {var subQ0=sQuery(id+"F0.wireOp",EDGE,"E0.bottom");Q21=makeQuery(id+"F7.boolean.opBoolean","SPLIT",EDGE,{"disambiguationData":[TD([makeQuery(id+"F7.opExtrude","SWEPT_FACE",FACE,{"disambiguationData":[OSD([sQuery(id+"F6.wireOp",EDGE,"E24.0.38.0")])]})])],"derivedFrom":makeQuery(id+"F1.opExtrude","CAP_EDGE",EDGE,{"disambiguationData":[OSD([subQ0])],"isStart":true})});}
            var Q22;
            {var subQ0=sQuery(id+"F0.wireOp",EDGE,"E0.bottom");Q22=makeQuery(id+"F7.boolean.opBoolean","SPLIT",EDGE,{"disambiguationData":[TD([makeQuery(id+"F7.opExtrude","SWEPT_FACE",FACE,{"disambiguationData":[OSD([sQuery(id+"F6.wireOp",EDGE,"E24.0.40.0")])]})])],"derivedFrom":makeQuery(id+"F1.opExtrude","CAP_EDGE",EDGE,{"disambiguationData":[OSD([subQ0])],"isStart":true})});}
            var Q23;
            {var subQ0=sQuery(id+"F0.wireOp",EDGE,"E0.bottom");Q23=makeQuery(id+"F7.boolean.opBoolean","SPLIT",EDGE,{"disambiguationData":[TD([makeQuery(id+"F7.opExtrude","SWEPT_FACE",FACE,{"disambiguationData":[OSD([sQuery(id+"F6.wireOp",EDGE,"E24.0.42.0")])]})])],"derivedFrom":makeQuery(id+"F1.opExtrude","CAP_EDGE",EDGE,{"disambiguationData":[OSD([subQ0])],"isStart":true})});}
            var Q24;
            {var subQ0=sQuery(id+"F0.wireOp",EDGE,"E0.bottom");Q24=makeQuery(id+"F7.boolean.opBoolean","SPLIT",EDGE,{"disambiguationData":[TD([makeQuery(id+"F7.opExtrude","SWEPT_FACE",FACE,{"disambiguationData":[OSD([sQuery(id+"F6.wireOp",EDGE,"E24.0.44.0")])]})])],"derivedFrom":makeQuery(id+"F1.opExtrude","CAP_EDGE",EDGE,{"disambiguationData":[OSD([subQ0])],"isStart":true})});}
            var Q25;
            {var subQ0=sQuery(id+"F0.wireOp",EDGE,"E0.bottom");Q25=makeQuery(id+"F7.boolean.opBoolean","SPLIT",EDGE,{"disambiguationData":[TD([makeQuery(id+"F7.opExtrude","SWEPT_FACE",FACE,{"disambiguationData":[OSD([sQuery(id+"F6.wireOp",EDGE,"E24.0.46.0")])]})])],"derivedFrom":makeQuery(id+"F1.opExtrude","CAP_EDGE",EDGE,{"disambiguationData":[OSD([subQ0])],"isStart":true})});}
            var Q26;
            {var subQ0=sQuery(id+"F0.wireOp",EDGE,"E0.bottom");Q26=makeQuery(id+"F7.boolean.opBoolean","SPLIT",EDGE,{"disambiguationData":[TD([makeQuery(id+"F7.opExtrude","SWEPT_FACE",FACE,{"disambiguationData":[OSD([sQuery(id+"F6.wireOp",EDGE,"E24.0.48.0")])]})])],"derivedFrom":makeQuery(id+"F1.opExtrude","CAP_EDGE",EDGE,{"disambiguationData":[OSD([subQ0])],"isStart":true})});}
            var Q27;
            {var subQ0=sQuery(id+"F0.wireOp",EDGE,"E0.bottom");Q27=makeQuery(id+"F7.boolean.opBoolean","SPLIT",EDGE,{"disambiguationData":[TD([makeQuery(id+"F7.opExtrude","SWEPT_FACE",FACE,{"disambiguationData":[OSD([sQuery(id+"F6.wireOp",EDGE,"E24.0.50.0")])]})])],"derivedFrom":makeQuery(id+"F1.opExtrude","CAP_EDGE",EDGE,{"disambiguationData":[OSD([subQ0])],"isStart":true})});}
            var Q28;
            {var subQ0=sQuery(id+"F0.wireOp",EDGE,"E0.bottom");Q28=makeQuery(id+"F7.boolean.opBoolean","SPLIT",EDGE,{"disambiguationData":[TD([makeQuery(id+"F7.opExtrude","SWEPT_FACE",FACE,{"disambiguationData":[OSD([sQuery(id+"F6.wireOp",EDGE,"E24.0.52.0")])]})])],"derivedFrom":makeQuery(id+"F1.opExtrude","CAP_EDGE",EDGE,{"disambiguationData":[OSD([subQ0])],"isStart":true})});}
            var Q29;
            {var subQ0=sQuery(id+"F0.wireOp",EDGE,"E0.bottom");Q29=makeQuery(id+"F7.boolean.opBoolean","SPLIT",EDGE,{"disambiguationData":[TD([makeQuery(id+"F7.opExtrude","SWEPT_FACE",FACE,{"disambiguationData":[OSD([sQuery(id+"F6.wireOp",EDGE,"E24.0.54.0")])]})])],"derivedFrom":makeQuery(id+"F1.opExtrude","CAP_EDGE",EDGE,{"disambiguationData":[OSD([subQ0])],"isStart":true})});}
            var Q30;
            {var subQ0=sQuery(id+"F0.wireOp",EDGE,"E0.bottom");Q30=makeQuery(id+"F7.boolean.opBoolean","SPLIT",EDGE,{"disambiguationData":[TD([makeQuery(id+"F7.opExtrude","SWEPT_FACE",FACE,{"disambiguationData":[OSD([sQuery(id+"F6.wireOp",EDGE,"E24.0.56.0")])]})])],"derivedFrom":makeQuery(id+"F1.opExtrude","CAP_EDGE",EDGE,{"disambiguationData":[OSD([subQ0])],"isStart":true})});}
            var Q31;
            {var subQ0=sQuery(id+"F0.wireOp",EDGE,"E0.bottom");var subQ1=sQuery(id+"F0.wireOp",EDGE,"E3.filletArc");Q31=makeQuery(id+"F7.boolean.opBoolean","SPLIT",EDGE,{"disambiguationData":[TD([makeQuery(id+"F1.opExtrude","SWEPT_FACE",FACE,{"disambiguationData":[OSD([subQ1])]})])],"derivedFrom":makeQuery(id+"F1.opExtrude","CAP_EDGE",EDGE,{"disambiguationData":[OSD([subQ0])],"isStart":true})});}
            var Q32;
            Q32=makeQuery(id+"F1.opExtrude","CAP_EDGE",EDGE,{"disambiguationData":[OSD([sQuery(id+"F0.wireOp",EDGE,"E0.left")])],"isStart":true});
            fillet(context, id + "F8", {"entities" : qUnion([Q0, Q1, Q2, Q3, Q4, Q5, Q6, Q7, Q8, Q9, Q10, Q11, Q12, Q13, Q14, Q15, Q16, Q17, Q18, Q19, Q20, Q21, Q22, Q23, Q24, Q25, Q26, Q27, Q28, Q29, Q30, Q31, Q32]), "radius" : 5 * mm, "tangentPropagation" : true, "allowEdgeOverflow" : false});
        }
        {
            var Q0;
            {var subQ0=sQuery(id+"F0.wireOp",EDGE,"E4.filletArc");var subQ1=sQuery(id+"F0.wireOp",EDGE,"E0.top");Q0=makeQuery(id+"F7.boolean.opBoolean","SPLIT",EDGE,{"disambiguationData":[TD([makeQuery(id+"F1.opExtrude","SWEPT_FACE",FACE,{"disambiguationData":[OSD([subQ1])]})])],"derivedFrom":makeQuery(id+"F1.opExtrude","CAP_EDGE",EDGE,{"disambiguationData":[OSD([subQ0])],"isStart":true})});}
            var Q1;
            {var subQ0=sQuery(id+"F0.wireOp",EDGE,"E4.filletArc");var subQ1=sQuery(id+"F0.wireOp",EDGE,"E0.top");Q1=makeQuery(id+"F7.boolean.opBoolean","SPLIT",EDGE,{"disambiguationData":[TD([makeQuery(id+"F1.opExtrude","SWEPT_FACE",FACE,{"disambiguationData":[OSD([subQ0])]})])],"derivedFrom":makeQuery(id+"F1.opExtrude","CAP_EDGE",EDGE,{"disambiguationData":[OSD([subQ1])],"isStart":true})});}
            var Q2;
            {var subQ0=sQuery(id+"F0.wireOp",EDGE,"E0.top");Q2=makeQuery(id+"F7.boolean.opBoolean","SPLIT",EDGE,{"disambiguationData":[TD([makeQuery(id+"F7.opExtrude","SWEPT_FACE",FACE,{"disambiguationData":[OSD([sQuery(id+"F6.wireOp",EDGE,"E24.0.54.0")])]})])],"derivedFrom":makeQuery(id+"F1.opExtrude","CAP_EDGE",EDGE,{"disambiguationData":[OSD([subQ0])],"isStart":true})});}
            var Q3;
            {var subQ0=sQuery(id+"F0.wireOp",EDGE,"E0.top");Q3=makeQuery(id+"F7.boolean.opBoolean","SPLIT",EDGE,{"disambiguationData":[TD([makeQuery(id+"F7.opExtrude","SWEPT_FACE",FACE,{"disambiguationData":[OSD([sQuery(id+"F6.wireOp",EDGE,"E24.0.52.0")])]})])],"derivedFrom":makeQuery(id+"F1.opExtrude","CAP_EDGE",EDGE,{"disambiguationData":[OSD([subQ0])],"isStart":true})});}
            var Q4;
            {var subQ0=sQuery(id+"F0.wireOp",EDGE,"E0.top");Q4=makeQuery(id+"F7.boolean.opBoolean","SPLIT",EDGE,{"disambiguationData":[TD([makeQuery(id+"F7.opExtrude","SWEPT_FACE",FACE,{"disambiguationData":[OSD([sQuery(id+"F6.wireOp",EDGE,"E24.0.50.0")])]})])],"derivedFrom":makeQuery(id+"F1.opExtrude","CAP_EDGE",EDGE,{"disambiguationData":[OSD([subQ0])],"isStart":true})});}
            var Q5;
            {var subQ0=sQuery(id+"F0.wireOp",EDGE,"E0.top");Q5=makeQuery(id+"F7.boolean.opBoolean","SPLIT",EDGE,{"disambiguationData":[TD([makeQuery(id+"F7.opExtrude","SWEPT_FACE",FACE,{"disambiguationData":[OSD([sQuery(id+"F6.wireOp",EDGE,"E24.0.48.0")])]})])],"derivedFrom":makeQuery(id+"F1.opExtrude","CAP_EDGE",EDGE,{"disambiguationData":[OSD([subQ0])],"isStart":true})});}
            var Q6;
            {var subQ0=sQuery(id+"F0.wireOp",EDGE,"E0.top");Q6=makeQuery(id+"F7.boolean.opBoolean","SPLIT",EDGE,{"disambiguationData":[TD([makeQuery(id+"F7.opExtrude","SWEPT_FACE",FACE,{"disambiguationData":[OSD([sQuery(id+"F6.wireOp",EDGE,"E24.0.46.0")])]})])],"derivedFrom":makeQuery(id+"F1.opExtrude","CAP_EDGE",EDGE,{"disambiguationData":[OSD([subQ0])],"isStart":true})});}
            var Q7;
            {var subQ0=sQuery(id+"F0.wireOp",EDGE,"E0.top");Q7=makeQuery(id+"F7.boolean.opBoolean","SPLIT",EDGE,{"disambiguationData":[TD([makeQuery(id+"F7.opExtrude","SWEPT_FACE",FACE,{"disambiguationData":[OSD([sQuery(id+"F6.wireOp",EDGE,"E24.0.44.0")])]})])],"derivedFrom":makeQuery(id+"F1.opExtrude","CAP_EDGE",EDGE,{"disambiguationData":[OSD([subQ0])],"isStart":true})});}
            var Q8;
            {var subQ0=sQuery(id+"F0.wireOp",EDGE,"E0.top");Q8=makeQuery(id+"F7.boolean.opBoolean","SPLIT",EDGE,{"disambiguationData":[TD([makeQuery(id+"F7.opExtrude","SWEPT_FACE",FACE,{"disambiguationData":[OSD([sQuery(id+"F6.wireOp",EDGE,"E24.0.42.0")])]})])],"derivedFrom":makeQuery(id+"F1.opExtrude","CAP_EDGE",EDGE,{"disambiguationData":[OSD([subQ0])],"isStart":true})});}
            var Q9;
            {var subQ0=sQuery(id+"F0.wireOp",EDGE,"E0.top");Q9=makeQuery(id+"F7.boolean.opBoolean","SPLIT",EDGE,{"disambiguationData":[TD([makeQuery(id+"F7.opExtrude","SWEPT_FACE",FACE,{"disambiguationData":[OSD([sQuery(id+"F6.wireOp",EDGE,"E24.0.40.0")])]})])],"derivedFrom":makeQuery(id+"F1.opExtrude","CAP_EDGE",EDGE,{"disambiguationData":[OSD([subQ0])],"isStart":true})});}
            var Q10;
            {var subQ0=sQuery(id+"F0.wireOp",EDGE,"E0.top");Q10=makeQuery(id+"F7.boolean.opBoolean","SPLIT",EDGE,{"disambiguationData":[TD([makeQuery(id+"F7.opExtrude","SWEPT_FACE",FACE,{"disambiguationData":[OSD([sQuery(id+"F6.wireOp",EDGE,"E24.0.38.0")])]})])],"derivedFrom":makeQuery(id+"F1.opExtrude","CAP_EDGE",EDGE,{"disambiguationData":[OSD([subQ0])],"isStart":true})});}
            var Q11;
            {var subQ0=sQuery(id+"F0.wireOp",EDGE,"E0.top");Q11=makeQuery(id+"F7.boolean.opBoolean","SPLIT",EDGE,{"disambiguationData":[TD([makeQuery(id+"F7.opExtrude","SWEPT_FACE",FACE,{"disambiguationData":[OSD([sQuery(id+"F6.wireOp",EDGE,"E24.0.36.0")])]})])],"derivedFrom":makeQuery(id+"F1.opExtrude","CAP_EDGE",EDGE,{"disambiguationData":[OSD([subQ0])],"isStart":true})});}
            var Q12;
            {var subQ0=sQuery(id+"F0.wireOp",EDGE,"E0.top");Q12=makeQuery(id+"F7.boolean.opBoolean","SPLIT",EDGE,{"disambiguationData":[TD([makeQuery(id+"F7.opExtrude","SWEPT_FACE",FACE,{"disambiguationData":[OSD([sQuery(id+"F6.wireOp",EDGE,"E24.0.34.0")])]})])],"derivedFrom":makeQuery(id+"F1.opExtrude","CAP_EDGE",EDGE,{"disambiguationData":[OSD([subQ0])],"isStart":true})});}
            var Q13;
            {var subQ0=sQuery(id+"F0.wireOp",EDGE,"E0.top");Q13=makeQuery(id+"F7.boolean.opBoolean","SPLIT",EDGE,{"disambiguationData":[TD([makeQuery(id+"F7.opExtrude","SWEPT_FACE",FACE,{"disambiguationData":[OSD([sQuery(id+"F6.wireOp",EDGE,"E24.0.32.0")])]})])],"derivedFrom":makeQuery(id+"F1.opExtrude","CAP_EDGE",EDGE,{"disambiguationData":[OSD([subQ0])],"isStart":true})});}
            var Q14;
            {var subQ0=sQuery(id+"F0.wireOp",EDGE,"E0.top");Q14=makeQuery(id+"F7.boolean.opBoolean","SPLIT",EDGE,{"disambiguationData":[TD([makeQuery(id+"F7.opExtrude","SWEPT_FACE",FACE,{"disambiguationData":[OSD([sQuery(id+"F6.wireOp",EDGE,"E24.0.30.0")])]})])],"derivedFrom":makeQuery(id+"F1.opExtrude","CAP_EDGE",EDGE,{"disambiguationData":[OSD([subQ0])],"isStart":true})});}
            var Q15;
            {var subQ0=sQuery(id+"F0.wireOp",EDGE,"E0.top");Q15=makeQuery(id+"F7.boolean.opBoolean","SPLIT",EDGE,{"disambiguationData":[TD([makeQuery(id+"F7.opExtrude","SWEPT_FACE",FACE,{"disambiguationData":[OSD([sQuery(id+"F6.wireOp",EDGE,"E24.0.28.0")])]})])],"derivedFrom":makeQuery(id+"F1.opExtrude","CAP_EDGE",EDGE,{"disambiguationData":[OSD([subQ0])],"isStart":true})});}
            var Q16;
            {var subQ0=sQuery(id+"F0.wireOp",EDGE,"E0.top");Q16=makeQuery(id+"F7.boolean.opBoolean","SPLIT",EDGE,{"disambiguationData":[TD([makeQuery(id+"F7.opExtrude","SWEPT_FACE",FACE,{"disambiguationData":[OSD([sQuery(id+"F6.wireOp",EDGE,"E24.0.26.0")])]})])],"derivedFrom":makeQuery(id+"F1.opExtrude","CAP_EDGE",EDGE,{"disambiguationData":[OSD([subQ0])],"isStart":true})});}
            var Q17;
            {var subQ0=sQuery(id+"F0.wireOp",EDGE,"E0.top");Q17=makeQuery(id+"F7.boolean.opBoolean","SPLIT",EDGE,{"disambiguationData":[TD([makeQuery(id+"F7.opExtrude","SWEPT_FACE",FACE,{"disambiguationData":[OSD([sQuery(id+"F6.wireOp",EDGE,"E24.0.24.0")])]})])],"derivedFrom":makeQuery(id+"F1.opExtrude","CAP_EDGE",EDGE,{"disambiguationData":[OSD([subQ0])],"isStart":true})});}
            var Q18;
            {var subQ0=sQuery(id+"F0.wireOp",EDGE,"E0.top");Q18=makeQuery(id+"F7.boolean.opBoolean","SPLIT",EDGE,{"disambiguationData":[TD([makeQuery(id+"F7.opExtrude","SWEPT_FACE",FACE,{"disambiguationData":[OSD([sQuery(id+"F6.wireOp",EDGE,"E24.0.22.0")])]})])],"derivedFrom":makeQuery(id+"F1.opExtrude","CAP_EDGE",EDGE,{"disambiguationData":[OSD([subQ0])],"isStart":true})});}
            var Q19;
            {var subQ0=sQuery(id+"F0.wireOp",EDGE,"E0.top");Q19=makeQuery(id+"F7.boolean.opBoolean","SPLIT",EDGE,{"disambiguationData":[TD([makeQuery(id+"F7.opExtrude","SWEPT_FACE",FACE,{"disambiguationData":[OSD([sQuery(id+"F6.wireOp",EDGE,"E24.0.20.0")])]})])],"derivedFrom":makeQuery(id+"F1.opExtrude","CAP_EDGE",EDGE,{"disambiguationData":[OSD([subQ0])],"isStart":true})});}
            var Q20;
            {var subQ0=sQuery(id+"F0.wireOp",EDGE,"E0.top");Q20=makeQuery(id+"F7.boolean.opBoolean","SPLIT",EDGE,{"disambiguationData":[TD([makeQuery(id+"F7.opExtrude","SWEPT_FACE",FACE,{"disambiguationData":[OSD([sQuery(id+"F6.wireOp",EDGE,"E23.16.0.0")])]})])],"derivedFrom":makeQuery(id+"F1.opExtrude","CAP_EDGE",EDGE,{"disambiguationData":[OSD([subQ0])],"isStart":true})});}
            var Q21;
            {var subQ0=sQuery(id+"F0.wireOp",EDGE,"E0.top");Q21=makeQuery(id+"F7.boolean.opBoolean","SPLIT",EDGE,{"disambiguationData":[TD([makeQuery(id+"F7.opExtrude","SWEPT_FACE",FACE,{"disambiguationData":[OSD([sQuery(id+"F6.wireOp",EDGE,"E23.18.0.0")])]})])],"derivedFrom":makeQuery(id+"F1.opExtrude","CAP_EDGE",EDGE,{"disambiguationData":[OSD([subQ0])],"isStart":true})});}
            var Q22;
            {var subQ0=sQuery(id+"F0.wireOp",EDGE,"E0.top");Q22=makeQuery(id+"F7.boolean.opBoolean","SPLIT",EDGE,{"disambiguationData":[TD([makeQuery(id+"F7.opExtrude","SWEPT_FACE",FACE,{"disambiguationData":[OSD([sQuery(id+"F6.wireOp",EDGE,"E23.14.0.0")])]})])],"derivedFrom":makeQuery(id+"F1.opExtrude","CAP_EDGE",EDGE,{"disambiguationData":[OSD([subQ0])],"isStart":true})});}
            var Q23;
            {var subQ0=sQuery(id+"F0.wireOp",EDGE,"E0.top");Q23=makeQuery(id+"F7.boolean.opBoolean","SPLIT",EDGE,{"disambiguationData":[TD([makeQuery(id+"F7.opExtrude","SWEPT_FACE",FACE,{"disambiguationData":[OSD([sQuery(id+"F6.wireOp",EDGE,"E23.12.0.0")])]})])],"derivedFrom":makeQuery(id+"F1.opExtrude","CAP_EDGE",EDGE,{"disambiguationData":[OSD([subQ0])],"isStart":true})});}
            var Q24;
            {var subQ0=sQuery(id+"F0.wireOp",EDGE,"E0.top");Q24=makeQuery(id+"F7.boolean.opBoolean","SPLIT",EDGE,{"disambiguationData":[TD([makeQuery(id+"F7.opExtrude","SWEPT_FACE",FACE,{"disambiguationData":[OSD([sQuery(id+"F6.wireOp",EDGE,"E23.10.0.0")])]})])],"derivedFrom":makeQuery(id+"F1.opExtrude","CAP_EDGE",EDGE,{"disambiguationData":[OSD([subQ0])],"isStart":true})});}
            var Q25;
            {var subQ0=sQuery(id+"F0.wireOp",EDGE,"E0.top");Q25=makeQuery(id+"F7.boolean.opBoolean","SPLIT",EDGE,{"disambiguationData":[TD([makeQuery(id+"F7.opExtrude","SWEPT_FACE",FACE,{"disambiguationData":[OSD([sQuery(id+"F6.wireOp",EDGE,"E23.8.0.0")])]})])],"derivedFrom":makeQuery(id+"F1.opExtrude","CAP_EDGE",EDGE,{"disambiguationData":[OSD([subQ0])],"isStart":true})});}
            var Q26;
            {var subQ0=sQuery(id+"F0.wireOp",EDGE,"E0.top");Q26=makeQuery(id+"F7.boolean.opBoolean","SPLIT",EDGE,{"disambiguationData":[TD([makeQuery(id+"F7.opExtrude","SWEPT_FACE",FACE,{"disambiguationData":[OSD([sQuery(id+"F6.wireOp",EDGE,"E23.6.0.0")])]})])],"derivedFrom":makeQuery(id+"F1.opExtrude","CAP_EDGE",EDGE,{"disambiguationData":[OSD([subQ0])],"isStart":true})});}
            var Q27;
            {var subQ0=sQuery(id+"F0.wireOp",EDGE,"E0.top");Q27=makeQuery(id+"F7.boolean.opBoolean","SPLIT",EDGE,{"disambiguationData":[TD([makeQuery(id+"F7.opExtrude","SWEPT_FACE",FACE,{"disambiguationData":[OSD([sQuery(id+"F6.wireOp",EDGE,"E23.4.0.0")])]})])],"derivedFrom":makeQuery(id+"F1.opExtrude","CAP_EDGE",EDGE,{"disambiguationData":[OSD([subQ0])],"isStart":true})});}
            var Q28;
            {var subQ0=sQuery(id+"F0.wireOp",EDGE,"E0.top");Q28=makeQuery(id+"F7.boolean.opBoolean","SPLIT",EDGE,{"disambiguationData":[TD([makeQuery(id+"F7.opExtrude","SWEPT_FACE",FACE,{"disambiguationData":[OSD([sQuery(id+"F6.wireOp",EDGE,"E23.2.0.0")])]})])],"derivedFrom":makeQuery(id+"F1.opExtrude","CAP_EDGE",EDGE,{"disambiguationData":[OSD([subQ0])],"isStart":true})});}
            fillet(context, id + "F9", {"entities" : qUnion([Q0, Q1, Q2, Q3, Q4, Q5, Q6, Q7, Q8, Q9, Q10, Q11, Q12, Q13, Q14, Q15, Q16, Q17, Q18, Q19, Q20, Q21, Q22, Q23, Q24, Q25, Q26, Q27, Q28]), "radius" : 5 * mm, "tangentPropagation" : true, "allowEdgeOverflow" : false});
        }
        {
            var Q0;
            Q0=makeQuery(id+"F1.opExtrude","SWEPT_BODY",BODY,{"disambiguationData":[OSD([sQuery(id+"F0.wireOp",EDGE,"E0.bottom"),sQuery(id+"F0.wireOp",EDGE,"E0.top"),sQuery(id+"F0.wireOp",EDGE,"E0.left"),sQuery(id+"F0.wireOp",EDGE,"E0.right"),sQuery(id+"F0.wireOp",EDGE,"E1.filletArc"),sQuery(id+"F0.wireOp",EDGE,"E2.filletArc"),sQuery(id+"F0.wireOp",EDGE,"E3.filletArc"),sQuery(id+"F0.wireOp",EDGE,"E4.filletArc")])]});
            transform(context, id + "F10", {"entities" : qUnion([Q0]), "transformType" : TransformType.TRANSLATION_3D, "dx" : 0 * mm, "dy" : 41 * mm, "dz" : -15 * mm, "makeCopy" : false});
        }
        {
            var Q0;
            Q0=makeQuery(id+"F1.opExtrude","SWEPT_BODY",BODY,{"disambiguationData":[OSD([sQuery(id+"F0.wireOp",EDGE,"E0.bottom"),sQuery(id+"F0.wireOp",EDGE,"E0.top"),sQuery(id+"F0.wireOp",EDGE,"E0.left"),sQuery(id+"F0.wireOp",EDGE,"E0.right"),sQuery(id+"F0.wireOp",EDGE,"E1.filletArc"),sQuery(id+"F0.wireOp",EDGE,"E2.filletArc"),sQuery(id+"F0.wireOp",EDGE,"E3.filletArc"),sQuery(id+"F0.wireOp",EDGE,"E4.filletArc")])]});
            var Q1;
            Q1=qCreatedBy(makeId("Top.planeOp"),FACE);
            mirror(context, id + "F11", {"entities" : qUnion([Q0]), "mirrorPlane" : qUnion([Q1])});
        }
    });
